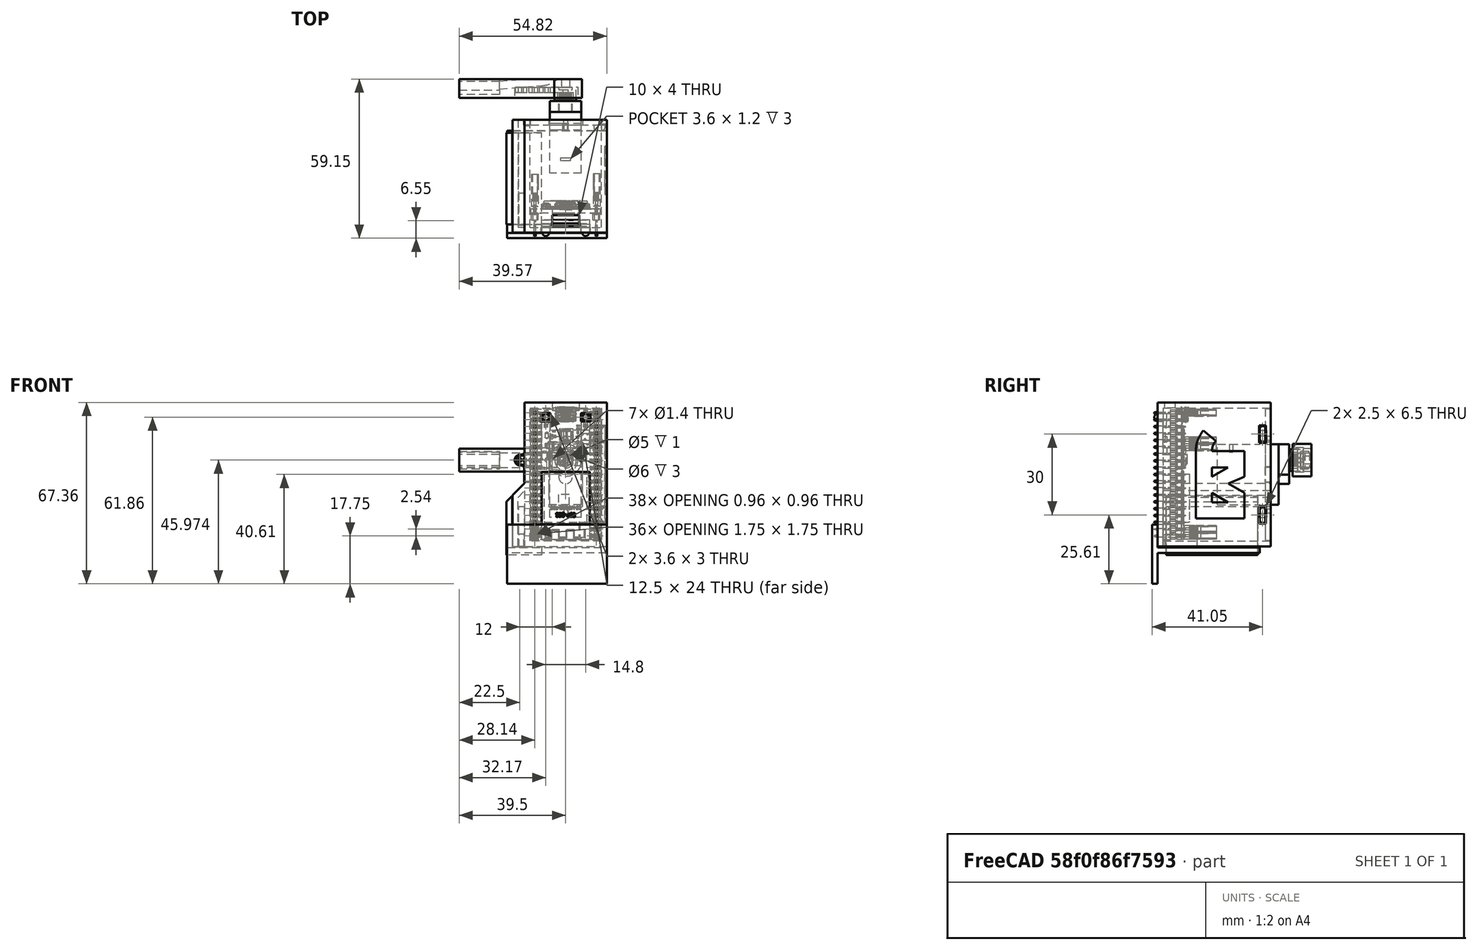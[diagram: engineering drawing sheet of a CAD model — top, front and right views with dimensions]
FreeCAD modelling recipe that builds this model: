
FCSTD DOCUMENT  (FreeCAD 0.18.4R)
Label: catdrainer_freecad
License: CreativeCommons Attribution-ShareAlike
LicenseURL: http://creativecommons.org/licenses/by-sa/4.0/
objects: Part::Feature×72, Sketcher::SketchObject×27, PartDesign::Pad×16, PartDesign::Pocket×11, PartDesign::Body×7, App::Part×2, Part::MultiFuse×2, PartDesign::AdditiveSphere×2, PartDesign::Fillet×1, Part::FeaturePython×1, Mesh::Feature×1, PartDesign::SubtractivePipe×1
note: 170 computed .brp shape members not serialized (recipe doc carries the construction recipe); baked Part::Feature solids carry a one-line shape summary decoded from their .brp

FEATURE [Part::Feature] Shape
  Placement = pos=(0.05,-0.05,0.75) rot=(0,0,1;0rad)
  shape: bbox 11.8 x 32.4 x 29.9 mm, 77 faces (baked)
FEATURE [Part::Feature] Part__Feature  label="ESP32S HW-573 PCB"
  shape: bbox 25.91 x 1.64 x 48.51 mm, 2018 faces (baked)
FEATURE [Part::Feature] Part__Feature001  label="ESP-WROOM-32"
  Placement = pos=(3e-15,1.565,-11.507) rot=(0,0.707107,0.707107;3.14159rad)
  shape: bbox 18.07 x 3.035 x 25.54 mm, 933 faces (baked)
FEATURE [Part::Feature] Part__Feature002  label="Male Header 19P 100 Pitch"
  Placement = pos=(11.43,-0.5,-0.005) rot=(0.57735,-0.57735,0.57735;2.0944rad)
  shape: bbox 2.54 x 11.54 x 47.96 mm, 648 faces (baked)
FEATURE [Part::Feature] Part__Feature003  label="Male Header 19P 100 Pitch001"
  Placement = pos=(-11.43,-0.5,-0.005) rot=(0.57735,-0.57735,0.57735;2.0944rad)
  shape: bbox 2.54 x 11.54 x 47.96 mm, 648 faces (baked)
FEATURE [Part::Feature] Part__Feature004  label="micro_usb_47346-0001"
  Placement = pos=(-1e-15,2.825,22.277) rot=(0,0,1;0rad)
  shape: bbox 7.98 x 2.94 x 5.43 mm, 394 faces (baked)
FEATURE [Part::Feature] Part__Feature005  label="CircuitWorks-SOT-223"
  Placement = pos=(4.374,2.38,6.453) rot=(0,1,0;1.5708rad)
  shape: bbox 6.96 x 1.68 x 6.5 mm, 86 faces (baked)
FEATURE [Part::Feature] Part__Feature006  label="Pol Cap SMD 3528 H2mm"
  Placement = pos=(-1.53686,1.6,5.5499) rot=(0,1,0;3.14159rad)
  shape: bbox 3.073 x 2.134 x 3.734 mm, 42 faces (baked)
FEATURE [Part::Feature] Part__Feature007  label="0805 SMD Capacitor"
  Placement = pos=(-6.069,1.6,6.903) rot=(0,-1,0;1.5708rad)
  shape: bbox 1.25 x 0.782 x 2 mm, 90 faces (baked)
FEATURE [Part::Feature] Part__Feature008  label="0603 SMD Resistor"
  Placement = pos=(-4.444,1.6,6.383) rot=(0,-1,0;1.5708rad)
  shape: bbox 0.8 x 0.302 x 1.6 mm, 90 faces (baked)
FEATURE [Part::Feature] Part__Feature009  label="SOT-23"
  Placement = pos=(7.19337,2.15,12.053) rot=(0,0,1;0rad)
  shape: bbox 3 x 1.1 x 2.5 mm, 49 faces (baked)
FEATURE [Part::Feature] Part__Feature010  label="QFN28_5X5"
  Placement = pos=(0.202,1.6,14.385) rot=(-0.57735,-0.57735,-0.57735;2.0944rad)
  shape: bbox 5.008 x 0.9445 x 5.008 mm, 254 faces, 31 solids (baked)
FEATURE [Part::Feature] Part__Feature011  label="SOT-024"
  Placement = pos=(7.19337,2.15,15.8743) rot=(0,0,1;0rad)
  shape: bbox 3 x 1.1 x 2.5 mm, 49 faces (baked)
FEATURE [Part::Feature] Part__Feature012  label="Tact Switch SMD Tab 4mmx3mm"
  Placement = pos=(-7.25,1.65,21.257) rot=(0,-1,0;1.5708rad)
  shape: bbox 3.001 x 2.301 x 5.001 mm, 101 faces, 3 solids (baked)
FEATURE [Part::Feature] Part__Feature013  label="Tact Switch SMD Tab 4mmx3mm001"
  Placement = pos=(7.35,1.65,21.257) rot=(0,-1,0;1.5708rad)
  shape: bbox 3.001 x 2.301 x 5.001 mm, 101 faces, 3 solids (baked)
FEATURE [Part::Feature] Part__Feature014  label="0402 SMD Resistor___ _________"
  Placement = pos=(4.684,1.58,10.4458) rot=(0,0,1;0rad)
  shape: bbox 1.042 x 0.3419 x 0.6019 mm, 289 faces, 3 solids (baked)
FEATURE [Part::Feature] Part__Feature015  label="0402 SMD Resistor___ _________001"
  Placement = pos=(4.684,1.58,18.0958) rot=(0,0,1;0rad)
  shape: bbox 1.042 x 0.3419 x 0.6019 mm, 289 faces, 3 solids (baked)
FEATURE [Part::Feature] Part__Feature016  label="0402 SMD Resistor___ _________002"
  Placement = pos=(4.684,1.58,16.9958) rot=(0,0,1;0rad)
  shape: bbox 1.042 x 0.3419 x 0.6019 mm, 289 faces, 3 solids (baked)
FEATURE [Part::Feature] Part__Feature017  label="0402 SMD Resistor___ _________003"
  Placement = pos=(4.514,1.58,15.5758) rot=(0,-1,0;1.5708rad)
  shape: bbox 0.6019 x 0.3419 x 1.042 mm, 289 faces, 3 solids (baked)
FEATURE [Part::Feature] Part__Feature018  label="0402 SMD Resistor___ _________004"
  Placement = pos=(4.514,1.58,12.0958) rot=(0,-1,0;1.5708rad)
  shape: bbox 0.6019 x 0.3419 x 1.042 mm, 289 faces, 3 solids (baked)
FEATURE [Part::Feature] Part__Feature019  label="0402 SMD Resistor___ _________005"
  Placement = pos=(4.514,1.58,13.8358) rot=(0,-1,0;1.5708rad)
  shape: bbox 0.6019 x 0.3419 x 1.042 mm, 289 faces, 3 solids (baked)
FEATURE [Part::Feature] Part__Feature020  label="LED SMD0603"
  Placement = pos=(-4.68116,1.59523,10.2006) rot=(-1,0,0;1.5708rad)
  shape: bbox 0.725 x 0.675 x 1.65 mm, 50 faces, 5 solids (baked)
FEATURE [Part::Feature] Part__Feature021  label="LED SMD0604"
  Placement = pos=(-7.23616,1.59523,10.2006) rot=(-1,0,0;1.5708rad)
  shape: bbox 0.725 x 0.675 x 1.65 mm, 50 faces, 5 solids (baked)
FEATURE [Part::Feature] Part__Feature022  label="0402 SMD Resistor___ _________006"
  Placement = pos=(-6.279,1.58,11.573) rot=(0,-1,0;1.5708rad)
  shape: bbox 0.6019 x 0.3419 x 1.042 mm, 289 faces, 3 solids (baked)
FEATURE [Part::Feature] Part__Feature023  label="0402 SMD Capacitor"
  Placement = pos=(-2.454,1.6,10.4668) rot=(0,0,1;0rad)
  shape: bbox 1 x 0.202 x 0.6 mm, 84 faces (baked)
FEATURE [Part::Feature] Part__Feature024  label="0402 SMD Resistor___ _________007"
  Placement = pos=(-2.434,1.6,9.3668) rot=(0,0,1;0rad)
  shape: bbox 1.042 x 0.3419 x 0.6019 mm, 289 faces, 3 solids (baked)
FEATURE [Part::Feature] Part__Feature025  label="0603 SMD Capacitor"
  Placement = pos=(-5.12,1.6,14.117) rot=(0,-1,0;1.5708rad)
  shape: bbox 0.8 x 0.302 x 1.6 mm, 90 faces (baked)
FEATURE [Part::Feature] Part__Feature026  label="0402 SMD Resistor___ _________008"
  Placement = pos=(-4.37,1.58,16.077) rot=(0,0,1;0rad)
  shape: bbox 1.042 x 0.3419 x 0.6019 mm, 289 faces, 3 solids (baked)
FEATURE [Part::Feature] Part__Feature027  label="0402 SMD Capacitor001"
  Placement = pos=(-3.9,1.6,14.097) rot=(0,1,0;1.5708rad)
  shape: bbox 0.6 x 0.202 x 1 mm, 84 faces (baked)
FEATURE [Part::Feature] Part__Feature028  label="SOD323F-1"
  Placement = pos=(-7.029,1.6,14.543) rot=(0.57735,-0.57735,-0.57735;4.18879rad)
  shape: bbox 1.35 x 1 x 2.5 mm, 29 faces (baked)
FEATURE [Part::Feature] Part__Feature029  label="Pin Solder Joint"
  Placement = pos=(11.43,1.62,22.86) rot=(0,0,1;0rad)
  shape: bbox 1.5 x 1.1 x 3 mm, 4 faces (baked)
FEATURE [Part::Feature] Part__Feature030  label="Pin Solder Joint001"
  Placement = pos=(-11.43,1.62,22.86) rot=(0,0,1;0rad)
  shape: bbox 1.5 x 1.1 x 3 mm, 4 faces (baked)
FEATURE [Part::Feature] Part__Feature031  label="Pin Solder Joint002"
  Placement = pos=(11.43,1.62,20.32) rot=(0,0,1;0rad)
  shape: bbox 1.5 x 1.1 x 3 mm, 4 faces (baked)
FEATURE [Part::Feature] Part__Feature032  label="Pin Solder Joint003"
  Placement = pos=(-11.43,1.62,20.32) rot=(0,0,1;0rad)
  shape: bbox 1.5 x 1.1 x 3 mm, 4 faces (baked)
FEATURE [Part::Feature] Part__Feature033  label="Pin Solder Joint004"
  Placement = pos=(11.43,1.62,17.78) rot=(0,0,1;0rad)
  shape: bbox 1.5 x 1.1 x 3 mm, 4 faces (baked)
FEATURE [Part::Feature] Part__Feature034  label="Pin Solder Joint005"
  Placement = pos=(-11.43,1.62,17.78) rot=(0,0,1;0rad)
  shape: bbox 1.5 x 1.1 x 3 mm, 4 faces (baked)
FEATURE [Part::Feature] Part__Feature035  label="Pin Solder Joint006"
  Placement = pos=(11.43,1.62,15.24) rot=(0,0,1;0rad)
  shape: bbox 1.5 x 1.1 x 3 mm, 4 faces (baked)
FEATURE [Part::Feature] Part__Feature036  label="Pin Solder Joint007"
  Placement = pos=(-11.43,1.62,15.24) rot=(0,0,1;0rad)
  shape: bbox 1.5 x 1.1 x 3 mm, 4 faces (baked)
FEATURE [Part::Feature] Part__Feature037  label="Pin Solder Joint008"
  Placement = pos=(11.43,1.62,12.7) rot=(0,0,1;0rad)
  shape: bbox 1.5 x 1.1 x 3 mm, 4 faces (baked)
FEATURE [Part::Feature] Part__Feature038  label="Pin Solder Joint009"
  Placement = pos=(-11.43,1.62,12.7) rot=(0,0,1;0rad)
  shape: bbox 1.5 x 1.1 x 3 mm, 4 faces (baked)
FEATURE [Part::Feature] Part__Feature039  label="Pin Solder Joint010"
  Placement = pos=(11.43,1.62,10.16) rot=(0,0,1;0rad)
  shape: bbox 1.5 x 1.1 x 3 mm, 4 faces (baked)
FEATURE [Part::Feature] Part__Feature040  label="Pin Solder Joint011"
  Placement = pos=(-11.43,1.62,10.16) rot=(0,0,1;0rad)
  shape: bbox 1.5 x 1.1 x 3 mm, 4 faces (baked)
FEATURE [Part::Feature] Part__Feature041  label="Pin Solder Joint012"
  Placement = pos=(11.43,1.62,7.62) rot=(0,0,1;0rad)
  shape: bbox 1.5 x 1.1 x 3 mm, 4 faces (baked)
FEATURE [Part::Feature] Part__Feature042  label="Pin Solder Joint013"
  Placement = pos=(-11.43,1.62,7.62) rot=(0,0,1;0rad)
  shape: bbox 1.5 x 1.1 x 3 mm, 4 faces (baked)
FEATURE [Part::Feature] Part__Feature043  label="Pin Solder Joint014"
  Placement = pos=(11.43,1.62,5.08) rot=(0,0,1;0rad)
  shape: bbox 1.5 x 1.1 x 3 mm, 4 faces (baked)
FEATURE [Part::Feature] Part__Feature044  label="Pin Solder Joint015"
  Placement = pos=(-11.43,1.62,5.08) rot=(0,0,1;0rad)
  shape: bbox 1.5 x 1.1 x 3 mm, 4 faces (baked)
FEATURE [Part::Feature] Part__Feature045  label="Pin Solder Joint016"
  Placement = pos=(11.43,1.62,2.54) rot=(0,0,1;0rad)
  shape: bbox 1.5 x 1.1 x 3 mm, 4 faces (baked)
FEATURE [Part::Feature] Part__Feature046  label="Pin Solder Joint017"
  Placement = pos=(-11.43,1.62,2.54) rot=(0,0,1;0rad)
  shape: bbox 1.5 x 1.1 x 3 mm, 4 faces (baked)
FEATURE [Part::Feature] Part__Feature047  label="Pin Solder Joint018"
  Placement = pos=(11.43,1.62,-3e-15) rot=(0,0,1;0rad)
  shape: bbox 1.5 x 1.1 x 3 mm, 4 faces (baked)
FEATURE [Part::Feature] Part__Feature048  label="Pin Solder Joint019"
  Placement = pos=(-11.43,1.62,-3e-15) rot=(0,0,1;0rad)
  shape: bbox 1.5 x 1.1 x 3 mm, 4 faces (baked)
FEATURE [Part::Feature] Part__Feature049  label="Pin Solder Joint020"
  Placement = pos=(11.43,1.62,-2.54) rot=(0,0,1;0rad)
  shape: bbox 1.5 x 1.1 x 3 mm, 4 faces (baked)
FEATURE [Part::Feature] Part__Feature050  label="Pin Solder Joint021"
  Placement = pos=(-11.43,1.62,-2.54) rot=(0,0,1;0rad)
  shape: bbox 1.5 x 1.1 x 3 mm, 4 faces (baked)
FEATURE [Part::Feature] Part__Feature051  label="Pin Solder Joint022"
  Placement = pos=(11.43,1.62,-5.08) rot=(0,0,1;0rad)
  shape: bbox 1.5 x 1.1 x 3 mm, 4 faces (baked)
FEATURE [Part::Feature] Part__Feature052  label="Pin Solder Joint023"
  Placement = pos=(-11.43,1.62,-5.08) rot=(0,0,1;0rad)
  shape: bbox 1.5 x 1.1 x 3 mm, 4 faces (baked)
FEATURE [Part::Feature] Part__Feature053  label="Pin Solder Joint024"
  Placement = pos=(11.43,1.62,-7.62) rot=(0,0,1;0rad)
  shape: bbox 1.5 x 1.1 x 3 mm, 4 faces (baked)
FEATURE [Part::Feature] Part__Feature054  label="Pin Solder Joint025"
  Placement = pos=(-11.43,1.62,-7.62) rot=(0,0,1;0rad)
  shape: bbox 1.5 x 1.1 x 3 mm, 4 faces (baked)
FEATURE [Part::Feature] Part__Feature055  label="Pin Solder Joint026"
  Placement = pos=(11.43,1.62,-10.16) rot=(0,0,1;0rad)
  shape: bbox 1.5 x 1.1 x 3 mm, 4 faces (baked)
FEATURE [Part::Feature] Part__Feature056  label="Pin Solder Joint027"
  Placement = pos=(-11.43,1.62,-10.16) rot=(0,0,1;0rad)
  shape: bbox 1.5 x 1.1 x 3 mm, 4 faces (baked)
FEATURE [Part::Feature] Part__Feature057  label="Pin Solder Joint028"
  Placement = pos=(11.43,1.62,-12.7) rot=(0,0,1;0rad)
  shape: bbox 1.5 x 1.1 x 3 mm, 4 faces (baked)
FEATURE [Part::Feature] Part__Feature058  label="Pin Solder Joint029"
  Placement = pos=(-11.43,1.62,-12.7) rot=(0,0,1;0rad)
  shape: bbox 1.5 x 1.1 x 3 mm, 4 faces (baked)
FEATURE [Part::Feature] Part__Feature059  label="Pin Solder Joint030"
  Placement = pos=(11.43,1.62,-15.24) rot=(0,0,1;0rad)
  shape: bbox 1.5 x 1.1 x 3 mm, 4 faces (baked)
FEATURE [Part::Feature] Part__Feature060  label="Pin Solder Joint031"
  Placement = pos=(-11.43,1.62,-15.24) rot=(0,0,1;0rad)
  shape: bbox 1.5 x 1.1 x 3 mm, 4 faces (baked)
FEATURE [Part::Feature] Part__Feature061  label="Pin Solder Joint032"
  Placement = pos=(11.43,1.62,-17.78) rot=(0,0,1;0rad)
  shape: bbox 1.5 x 1.1 x 3 mm, 4 faces (baked)
FEATURE [Part::Feature] Part__Feature062  label="Pin Solder Joint033"
  Placement = pos=(-11.43,1.62,-17.78) rot=(0,0,1;0rad)
  shape: bbox 1.5 x 1.1 x 3 mm, 4 faces (baked)
FEATURE [Part::Feature] Part__Feature063  label="Pin Solder Joint034"
  Placement = pos=(11.43,1.62,-20.32) rot=(0,0,1;0rad)
  shape: bbox 1.5 x 1.1 x 3 mm, 4 faces (baked)
FEATURE [Part::Feature] Part__Feature064  label="Pin Solder Joint035"
  Placement = pos=(-11.43,1.62,-20.32) rot=(0,0,1;0rad)
  shape: bbox 1.5 x 1.1 x 3 mm, 4 faces (baked)
FEATURE [Part::Feature] Part__Feature065  label="Pin Solder Joint036"
  Placement = pos=(11.43,1.62,-22.86) rot=(0,0,1;0rad)
  shape: bbox 1.5 x 1.1 x 3 mm, 4 faces (baked)
FEATURE [Part::Feature] Part__Feature066  label="Pin Solder Joint037"
  Placement = pos=(-11.43,1.62,-22.86) rot=(0,0,1;0rad)
  shape: bbox 1.5 x 1.1 x 3 mm, 4 faces (baked)
FEATURE [App::Part] ESP32S_Dev_Board_0_9inch_width_ASSY  label="ESP32S Dev Board 0.9inch width ASSY"
  Group = -> [Part__Feature,Part__Feature001,Part__Feature002,Part__Feature003,Part__Feature004,Part__Feature005,Part__Feature006,Part__Feature007,Part__Feature008,Part__Feature009,Part__Feature010,Part__Feature011,Part__Feature012,Part__Feature013,Part__Feature014,Part__Feature015,Part__Feature016,Part__Feature017,Part__Feature018,Part__Feature019,Part__Feature020,Part__Feature021,Part__Feature022,+44 more]
  Origin = -> Origin
  Placement = pos=(0,0,0) rot=(0,0,1;3.14159rad)
FEATURE [Part::Feature] Shape003  label="5v"
  Placement = pos=(-11.45,-14.6,22.9) rot=(0.57735,0.57735,0.57735;4.18879rad)
  shape: bbox 2.54 x 12 x 2.54 mm, 49 faces, 2 solids (baked)
FEATURE [Part::Feature] Shape006  label="laserplug"
  Placement = pos=(11.45,-14.55,-20.3) rot=(0.57735,-0.57735,-0.57735;4.18879rad)
  shape: bbox 2.54 x 12 x 5.08 mm, 98 faces, 4 solids (baked)
FEATURE [Part::Feature] Shape005  label="Servoplug"
  Placement = pos=(-11.45,-14.6,10.15) rot=(0.57735,0.57735,0.57735;4.18879rad)
  shape: bbox 2.54 x 12 x 5.08 mm, 98 faces, 4 solids (baked)
FEATURE [Part::MultiFuse] Fusion  label="pins"
  Placement = pos=(0,0,0) rot=(0,0,1;3.14159rad)
  Refine = true
  Shapes = -> [Shape006,Shape003,Shape005]
FEATURE [Sketcher::SketchObject] Sketch
  MapMode = 5
  Placement = pos=(0,0,0) rot=(0.57735,0.57735,0.57735;2.0944rad)
  Support = -> [YZ_Plane002]
  sketch-geometry (7):
    g0: LineSegment StartX=-4 StartY=22.5 StartZ=0 EndX=-4 EndY=20 EndZ=0
    g1: LineSegment StartX=-4 StartY=20 StartZ=0 EndX=-4.75 EndY=10 EndZ=0
    g2: LineSegment StartX=-4.75 StartY=10 StartZ=0 EndX=-5.25 EndY=10 EndZ=0
    g3: LineSegment StartX=-4 StartY=22.5 StartZ=0 EndX=-7.25 EndY=22.5 EndZ=0
    g4: LineSegment StartX=-5.25 StartY=10 StartZ=0 EndX=-5.25 EndY=20 EndZ=0
    g5: LineSegment StartX=-5.25 StartY=20 StartZ=0 EndX=-7.25 EndY=20 EndZ=0
    g6: LineSegment StartX=-7.25 StartY=20 StartZ=0 EndX=-7.25 EndY=22.5 EndZ=0
  constraints (21):
    c: Vertical(g0)
    c: Coincident(g0,g1)
    c: Coincident(g1,g2)
    c: Horizontal(g2)
    c: Coincident(g3,g0)
    c: Horizontal(g3)
    c: DistanceY(g0,g0) = 2.5
    c: DistanceX(g2,g2) = 0.5
    c: DistanceX(g3,g3) = 3.25
    c: DistanceX(g1) = -4.75
    c: DistanceY(g1) = 10
    c: Coincident(g2,g4)
    c: Vertical(g4)
    c: Coincident(g4,g5)
    c: Horizontal(g5)
    c: Coincident(g5,g6)
    c: Vertical(g6)
    c: DistanceX(g5,g5) = 2
    c: Coincident(g3,g6)
    c: DistanceY(g6,g6) = 2.5
    c: DistanceY(g4,g4) = 10
FEATURE [PartDesign::Pad] Pad
  Length = 18
  Length2 = 100
  Midplane = true
  Placement = pos=(0,0,0) rot=(0.57735,0.57735,0.57735;2.0944rad)
  Profile = -> Sketch
  Refine = true
  Type = 0
FEATURE [Sketcher::SketchObject] Sketch001
  ExternalGeometry = -> [Pad]
  MapMode = 5
  Placement = pos=(-3.2e-15,-7.25,1.6e-15) rot=(-0.57735,-0.57735,0.57735;4.18879rad)
  Support = -> [Pad]
  sketch-geometry (4):
    g0: LineSegment StartX=-22.5 StartY=5.8 StartZ=0 EndX=-12 EndY=5.8 EndZ=0
    g1: LineSegment StartX=-12 StartY=5.8 StartZ=0 EndX=-12 EndY=-5.8 EndZ=0
    g2: LineSegment StartX=-12 StartY=-5.8 StartZ=0 EndX=-22.5 EndY=-5.8 EndZ=0
    g3: LineSegment StartX=-22.5 StartY=-5.8 StartZ=0 EndX=-22.5 EndY=5.8 EndZ=0
  constraints (11):
    c: Coincident(g0,g1)
    c: Coincident(g1,g2)
    c: Coincident(g2,g3)
    c: Coincident(g3,g0)
    c: Horizontal(g0)
    c: Horizontal(g2)
    c: Vertical(g1)
    c: Distance(g1,g-3) = 2
    c: Symmetric(g0,g2,g-1)
    c: DistanceY(g-4,g2) = 3.2
    c: PointOnObject(g2,g-5)
FEATURE [PartDesign::Pocket] Pocket
  BaseFeature = -> Pad
  Length = 5
  Length2 = 100
  Placement = pos=(0,0,0) rot=(0.57735,0.57735,0.57735;2.0944rad)
  Profile = -> Sketch001
  Refine = true
  Type = 0
FEATURE [Sketcher::SketchObject] Sketch002
  MapMode = 5
  Placement = pos=(-3e-15,-7.25,5e-15) rot=(0.57735,0.57735,-0.57735;2.0944rad)
  sketch-geometry (16):
    g0: LineSegment StartX=-26.75 StartY=15.25 StartZ=0 EndX=-26.75 EndY=-15.25 EndZ=0
    g1: LineSegment StartX=-26.75 StartY=-15.25 StartZ=0 EndX=26.75 EndY=-15.25 EndZ=0
    g2: LineSegment StartX=26.75 StartY=-15.25 StartZ=0 EndX=26.75 EndY=15.25 EndZ=0
    g3: LineSegment StartX=26.75 StartY=15.25 StartZ=0 EndX=-26.75 EndY=15.25 EndZ=0
    g4: LineSegment StartX=-1 StartY=9 StartZ=0 EndX=18.5 EndY=9 EndZ=0
    g5: LineSegment StartX=18.5 StartY=9 StartZ=0 EndX=18.5 EndY=-9 EndZ=0
    g6: LineSegment StartX=18.5 StartY=-9 StartZ=0 EndX=-1 EndY=-9 EndZ=0
    g7: LineSegment StartX=-1 StartY=-9 StartZ=0 EndX=-1 EndY=9 EndZ=0
    g8: LineSegment StartX=-22.75 StartY=9.2 StartZ=0 EndX=-19.75 EndY=9.2 EndZ=0
    g9: LineSegment StartX=-19.75 StartY=9.2 StartZ=0 EndX=-19.75 EndY=5.6 EndZ=0
    g10: LineSegment StartX=-19.75 StartY=5.6 StartZ=0 EndX=-22.75 EndY=5.6 EndZ=0
    g11: LineSegment StartX=-22.75 StartY=5.6 StartZ=0 EndX=-22.75 EndY=9.2 EndZ=0
    g12: LineSegment StartX=-22.75 StartY=-5.6 StartZ=0 EndX=-19.75 EndY=-5.6 EndZ=0
    g13: LineSegment StartX=-19.75 StartY=-5.6 StartZ=0 EndX=-19.75 EndY=-9.2 EndZ=0
    g14: LineSegment StartX=-19.75 StartY=-9.2 StartZ=0 EndX=-22.75 EndY=-9.2 EndZ=0
    g15: LineSegment StartX=-22.75 StartY=-9.2 StartZ=0 EndX=-22.75 EndY=-5.6 EndZ=0
  constraints (44):
    c: Coincident(g0,g1)
    c: Horizontal(g1)
    c: Coincident(g1,g2)
    c: Vertical(g2)
    c: Coincident(g2,g3)
    c: Coincident(g0,g3)
    c: Symmetric(g0,g0,g-1)
    c: DistanceY(g0,g0) = 30.5
    c: DistanceX(g3,g3) = 53.5
    c: Coincident(g5,g6)
    c: Coincident(g6,g7)
    c: Coincident(g7,g4)
    c: Horizontal(g4)
    c: Horizontal(g6)
    c: Vertical(g7)
    c: Symmetric(g4,g5,g-1)
    c: DistanceY(g4) = 9
    c: Coincident(g4,g5)
    c: DistanceX(g6,g6) = 19.5
    c: Coincident(g8,g9)
    c: Coincident(g9,g10)
    c: Coincident(g10,g11)
    c: Coincident(g11,g8)
    c: Horizontal(g8)
    c: Horizontal(g10)
    c: Vertical(g9)
    c: Vertical(g11)
    c: Coincident(g12,g13)
    c: Coincident(g13,g14)
    c: Coincident(g14,g15)
    c: Coincident(g15,g12)
    c: Horizontal(g12)
    c: Horizontal(g14)
    c: Vertical(g13)
    c: Vertical(g15)
    c: Symmetric(g9,g12,g-1)
    c: DistanceY(g13,g13) = 3.6
    c: DistanceY(g12) = -5.6
    c: DistanceX(g12,g12) = 3
    c: Equal(g15,g11)
    c: Equal(g12,g8)
    c: Symmetric(g2,g0,g-2)
    c: DistanceX(g12,g-1) = 19.75
    c: DistanceX(g6,g-1) = 1
FEATURE [PartDesign::Pad] Pad001  label="Base"
  Length = 2
  Length2 = 100
  Placement = pos=(-3e-15,-7.25,5e-15) rot=(0.57735,0.57735,-0.57735;2.0944rad)
  Profile = -> Sketch002
  Refine = true
  Reversed = true
  Type = 0
FEATURE [Sketcher::SketchObject] Sketch003
  ExternalGeometry = -> [Pad001]
  MapMode = 5
  Placement = pos=(1.4e-15,-5.25,4.3e-15) rot=(-0.57735,0.57735,0.57735;2.0944rad)
  Support = -> [Pad001]
  sketch-geometry (9):
    g0: LineSegment StartX=-14.15 StartY=-5.625 StartZ=0 EndX=-12.15 EndY=-5.625 EndZ=0
    g1: LineSegment StartX=-12.15 StartY=-5.625 StartZ=0 EndX=-12.15 EndY=5.625 EndZ=0
    g2: LineSegment StartX=-12.15 StartY=5.625 StartZ=0 EndX=-14.15 EndY=5.625 EndZ=0
    g3: LineSegment StartX=-14.15 StartY=5.625 StartZ=0 EndX=-14.15 EndY=-5.625 EndZ=0
    g4: LineSegment StartX=-9.9 StartY=-9 StartZ=0 EndX=-7.9 EndY=-9 EndZ=0
    g5: LineSegment StartX=-7.9 StartY=-9 StartZ=0 EndX=-7.9 EndY=9 EndZ=0
    g6: LineSegment StartX=-7.9 StartY=9 StartZ=0 EndX=-9.9 EndY=9 EndZ=0
    g7: LineSegment StartX=-9.9 StartY=9 StartZ=0 EndX=-9.9 EndY=-9 EndZ=0
    g8: LineSegment [constr] StartX=-12.15 StartY=5.625 StartZ=0 EndX=-9.9 EndY=5.625 EndZ=0
  constraints (25):
    c: Coincident(g0,g1)
    c: Coincident(g1,g2)
    c: Coincident(g2,g3)
    c: Coincident(g3,g0)
    c: Horizontal(g0)
    c: Horizontal(g2)
    c: Vertical(g3)
    c: Coincident(g4,g5)
    c: Coincident(g5,g6)
    c: Coincident(g6,g7)
    c: Coincident(g7,g4)
    c: Horizontal(g4)
    c: Horizontal(g6)
    c: Vertical(g7)
    c: Equal(g6,g2)
    c: DistanceX(g6,g6) = 2
    c: DistanceX(g5,g-3) = 6.9
    c: PointOnObject(g8,g7)
    c: Horizontal(g8)
    c: Symmetric(g4,g5,g-1)
    c: DistanceY(g5,g5) = 18
    c: Symmetric(g1,g0,g-1)
    c: DistanceY(g1,g1) = 11.25
    c: DistanceX(g8,g8) = 2.25
    c: Coincident(g8,g1)
FEATURE [PartDesign::Pad] Pad002  label="buton_tabs"
  BaseFeature = -> Pad001
  Length = 1.5
  Length2 = 100
  Placement = pos=(-3e-15,-7.25,5e-15) rot=(0.57735,0.57735,-0.57735;2.0944rad)
  Profile = -> Sketch003
  Refine = true
  Type = 0
FEATURE [Sketcher::SketchObject] Sketch004
  ExternalGeometry = -> [Pad002]
  MapMode = 5
  Placement = pos=(3.4e-15,-5.25,4.3e-15) rot=(-0.57735,0.57735,0.57735;2.0944rad)
  Support = -> [Pad002]
  sketch-geometry (5):
    g0: LineSegment StartX=18.5 StartY=9 StartZ=0 EndX=24.25 EndY=9 EndZ=0
    g1: LineSegment StartX=24.25 StartY=9 StartZ=0 EndX=24.25 EndY=-9 EndZ=0
    g2: LineSegment StartX=24.25 StartY=-9 StartZ=0 EndX=18.5 EndY=-9 EndZ=0
    g3: LineSegment StartX=18.5 StartY=-9 StartZ=0 EndX=18.5 EndY=9 EndZ=0
    g4: LineSegment [constr] StartX=24.25 StartY=9 StartZ=0 EndX=26.75 EndY=9 EndZ=0
  constraints (13):
    c: Coincident(g0,g1)
    c: Coincident(g1,g2)
    c: Coincident(g2,g3)
    c: Coincident(g3,g0)
    c: Horizontal(g0)
    c: Horizontal(g2)
    c: Vertical(g1)
    c: Coincident(g0,g-3)
    c: Coincident(g4,g0)
    c: PointOnObject(g4,g-4)
    c: Horizontal(g4)
    c: DistanceX(g4,g4) = 2.5
    c: Coincident(g2,g-3)
FEATURE [PartDesign::Pad] Pad003  label="antenna_bump"
  BaseFeature = -> Pad002
  Length = 2.75
  Length2 = 100
  Placement = pos=(-3e-15,-7.25,5e-15) rot=(0.57735,0.57735,-0.57735;2.0944rad)
  Profile = -> Sketch004
  Refine = true
  Type = 0
FEATURE [Sketcher::SketchObject] Sketch005
  ExternalGeometry = -> [Pad003]
  MapMode = 5
  Placement = pos=(5.4e-15,-5.25,4.3e-15) rot=(-0.57735,0.57735,0.57735;2.0944rad)
  Support = -> [Pad003]
  sketch-geometry (8):
    g0: LineSegment StartX=26.75 StartY=-15.25 StartZ=0 EndX=-26.75 EndY=-15.25 EndZ=0
    g1: LineSegment StartX=-26.75 StartY=-15.25 StartZ=0 EndX=-26.75 EndY=15.25 EndZ=0
    g2: LineSegment StartX=-26.75 StartY=15.25 StartZ=0 EndX=26.75 EndY=15.25 EndZ=0
    g3: LineSegment StartX=26.75 StartY=15.25 StartZ=0 EndX=26.75 EndY=-15.25 EndZ=0
    g4: LineSegment StartX=-24.75 StartY=-13.25 StartZ=0 EndX=24.75 EndY=-13.25 EndZ=0
    g5: LineSegment StartX=24.75 StartY=-13.25 StartZ=0 EndX=24.75 EndY=13.25 EndZ=0
    g6: LineSegment StartX=24.75 StartY=13.25 StartZ=0 EndX=-24.75 EndY=13.25 EndZ=0
    g7: LineSegment StartX=-24.75 StartY=13.25 StartZ=0 EndX=-24.75 EndY=-13.25 EndZ=0
  constraints (19):
    c: Coincident(g0,g1)
    c: Coincident(g1,g2)
    c: Coincident(g6,g7)
    c: Coincident(g5,g6)
    c: Coincident(g4,g5)
    c: Coincident(g4,g7)
    c: Coincident(g0,g3)
    c: Coincident(g2,g3)
    c: Coincident(g0,g-3)
    c: Coincident(g2,g-3)
    c: Coincident(g1,g-4)
    c: Coincident(g0,g-4)
    c: Vertical(g5)
    c: Horizontal(g6)
    c: Horizontal(g4)
    c: Vertical(g7)
    c: Symmetric(g6,g4,g-1)
    c: Distance(g5,g3) = 2
    c: DistanceY(g5,g2) = 2
FEATURE [PartDesign::Pad] Pad004  label="Walls"
  BaseFeature = -> Pad003
  Length = 40
  Length2 = 100
  Placement = pos=(-3e-15,-7.25,5e-15) rot=(0.57735,0.57735,-0.57735;2.0944rad)
  Profile = -> Sketch005
  Refine = true
  Type = 0
FEATURE [Sketcher::SketchObject] Sketch006
  MapMode = 5
  Placement = pos=(1.53493e-10,-7.25,26.75) rot=(0,0,1;3.14159rad)
  Support = -> [Pad004]
  sketch-geometry (4):
    g0: LineSegment StartX=-5 StartY=-2.5 StartZ=0 EndX=5 EndY=-2.5 EndZ=0
    g1: LineSegment StartX=5 StartY=-2.5 StartZ=0 EndX=5 EndY=-6.5 EndZ=0
    g2: LineSegment StartX=5 StartY=-6.5 StartZ=0 EndX=-5 EndY=-6.5 EndZ=0
    g3: LineSegment StartX=-5 StartY=-6.5 StartZ=0 EndX=-5 EndY=-2.5 EndZ=0
  constraints (11):
    c: Coincident(g0,g3)
    c: Coincident(g0,g1)
    c: Coincident(g1,g2)
    c: Coincident(g2,g3)
    c: DistanceY(g1,g1) = 4
    c: DistanceX(g2,g2) = 10
    c: Equal(g1,g3)
    c: Vertical(g1)
    c: Vertical(g3)
    c: Symmetric(g0,g0,g-2)
    c: DistanceY(g0,g-1) = 2.5
FEATURE [PartDesign::Pocket] Pocket001  label="USB Opening"
  BaseFeature = -> Pad004
  Length = 2
  Length2 = 100
  Placement = pos=(-3e-15,-7.25,5e-15) rot=(0.57735,0.57735,-0.57735;2.0944rad)
  Profile = -> Sketch006
  Refine = true
  Type = 0
FEATURE [Sketcher::SketchObject] Sketch008  label="two_lid_clips"
  ExternalGeometry = -> [Pocket001]
  MapMode = 5
  Placement = pos=(15.25,-7.25,-8.51e-12) rot=(0.707107,0,0.707107;3.14159rad)
  Support = -> [Pocket001]
  sketch-geometry (8):
    g0: LineSegment StartX=-18.25 StartY=-37.75 StartZ=0 EndX=-11.75 EndY=-37.75 EndZ=0
    g1: LineSegment StartX=-11.75 StartY=-37.75 StartZ=0 EndX=-11.75 EndY=-40.25 EndZ=0
    g2: LineSegment StartX=-11.75 StartY=-40.25 StartZ=0 EndX=-18.25 EndY=-40.25 EndZ=0
    g3: LineSegment StartX=-18.25 StartY=-40.25 StartZ=0 EndX=-18.25 EndY=-37.75 EndZ=0
    g4: LineSegment StartX=11.75 StartY=-37.75 StartZ=0 EndX=18.25 EndY=-37.75 EndZ=0
    g5: LineSegment StartX=18.25 StartY=-37.75 StartZ=0 EndX=18.25 EndY=-40.25 EndZ=0
    g6: LineSegment StartX=18.25 StartY=-40.25 StartZ=0 EndX=11.75 EndY=-40.25 EndZ=0
    g7: LineSegment StartX=11.75 StartY=-40.25 StartZ=0 EndX=11.75 EndY=-37.75 EndZ=0
  constraints (23):
    c: Coincident(g0,g1)
    c: Coincident(g1,g2)
    c: Coincident(g2,g3)
    c: Coincident(g3,g0)
    c: Horizontal(g0)
    c: Horizontal(g2)
    c: Vertical(g1)
    c: Vertical(g3)
    c: Coincident(g4,g5)
    c: Coincident(g5,g6)
    c: Coincident(g6,g7)
    c: Coincident(g7,g4)
    c: Horizontal(g4)
    c: Horizontal(g6)
    c: Vertical(g5)
    c: Vertical(g7)
    c: Equal(g4,g0)
    c: Equal(g7,g1)
    c: DistanceY(g5,g5) = 2.5
    c: DistanceX(g6,g6) = 6.5
    c: Symmetric(g6,g1,g-2)
    c: Distance(g5,g-3) = 1.75
    c: DistanceX(g1,g6) = 23.5
FEATURE [PartDesign::Pocket] Pocket002  label="lid_clip_opening"
  BaseFeature = -> Pocket001
  Length = 5
  Length2 = 100
  Placement = pos=(-3e-15,-7.25,5e-15) rot=(0.57735,0.57735,-0.57735;2.0944rad)
  Profile = -> Sketch008
  Refine = true
  Type = 0
FEATURE [Sketcher::SketchObject] Sketch009
  AttachmentOffset = pos=(0,0,32.75) rot=(0,0,1;0rad)
  MapMode = 5
  Placement = pos=(0,32.75,7.3e-15) rot=(0,0.707107,0.707107;3.14159rad)
  Support = -> [XZ_Plane004]
  sketch-geometry (9):
    g0: LineSegment StartX=13 StartY=24.5 StartZ=0 EndX=-13 EndY=24.5 EndZ=0
    g1: LineSegment StartX=-13 StartY=24.5 StartZ=0 EndX=-13 EndY=-24.5 EndZ=0
    g2: LineSegment StartX=-13 StartY=-24.5 StartZ=0 EndX=13 EndY=-24.5 EndZ=0
    g3: LineSegment StartX=13 StartY=24.5 StartZ=0 EndX=13 EndY=2.75 EndZ=0
    g4: LineSegment StartX=13 StartY=2.75 StartZ=0 EndX=15.4 EndY=2.75 EndZ=0
    g5: LineSegment StartX=15.4 StartY=2.75 StartZ=0 EndX=15.4 EndY=-2.75 EndZ=0
    g6: LineSegment StartX=15.4 StartY=-2.75 StartZ=0 EndX=13 EndY=-2.75 EndZ=0
    g7: LineSegment StartX=13 StartY=-2.75 StartZ=0 EndX=13 EndY=-24.5 EndZ=0
    g8: LineSegment [constr] StartX=13 StartY=2.75 StartZ=0 EndX=13 EndY=-2.75 EndZ=0
  constraints (24):
    c: Coincident(g0,g1)
    c: Coincident(g1,g2)
    c: Horizontal(g0)
    c: Horizontal(g2)
    c: Vertical(g1)
    c: Symmetric(g0,g2,g-1)
    c: DistanceX(g0,g0) = 26
    c: DistanceY(g1,g1) = 49
    c: Coincident(g0,g3)
    c: Vertical(g3)
    c: Coincident(g3,g4)
    c: Coincident(g4,g5)
    c: Coincident(g5,g6)
    c: Horizontal(g6)
    c: Coincident(g6,g7)
    c: Coincident(g7,g2)
    c: Vertical(g7)
    c: Horizontal(g4)
    c: DistanceY(g5,g5) = 5.5
    c: Symmetric(g4,g5,g-1)
    c: Coincident(g8,g3)
    c: Coincident(g8,g6)
    c: Vertical(g8)
    c: DistanceX(g4,g4) = 2.4
FEATURE [PartDesign::Pad] Pad005
  Length = 2
  Length2 = 100
  Placement = pos=(0,0,0) rot=(1,0,0;1.5708rad)
  Profile = -> Sketch009
  Refine = true
  Type = 0
FEATURE [Sketcher::SketchObject] Sketch010
  ExternalGeometry = -> [Pocket002]
  MapMode = 5
  Placement = pos=(-15.25,-7.25,7.599e-13) rot=(-0.707107,0,0.707107;3.14159rad)
  Support = -> [Pocket002]
  sketch-geometry (4):
    g0: LineSegment StartX=-2.875 StartY=-39.85 StartZ=0 EndX=2.875 EndY=-39.85 EndZ=0
    g1: LineSegment StartX=2.875 StartY=-39.85 StartZ=0 EndX=2.875 EndY=-42 EndZ=0
    g2: LineSegment StartX=2.875 StartY=-42 StartZ=0 EndX=-2.875 EndY=-42 EndZ=0
    g3: LineSegment StartX=-2.875 StartY=-42 StartZ=0 EndX=-2.875 EndY=-39.85 EndZ=0
  constraints (11):
    c: Coincident(g2,g3)
    c: Coincident(g1,g2)
    c: Coincident(g0,g3)
    c: Coincident(g0,g1)
    c: Symmetric(g0,g0,g-2)
    c: Vertical(g1)
    c: Vertical(g3)
    c: Horizontal(g2)
    c: DistanceX(g2,g2) = 5.75
    c: DistanceY(g1,g1) = 2.15
    c: PointOnObject(g1,g-3)
FEATURE [PartDesign::Pocket] Pocket003  label="Latch_tab_hole"
  BaseFeature = -> Pocket002
  Length = 5
  Length2 = 100
  Placement = pos=(-3e-15,-7.25,5e-15) rot=(0.57735,0.57735,-0.57735;2.0944rad)
  Profile = -> Sketch010
  Refine = true
  Type = 0
FEATURE [Sketcher::SketchObject] Sketch011
  ExternalGeometry = -> [Pad005]
  MapMode = 5
  Placement = pos=(0,32.75,-9.5e-15) rot=(1,0,0;1.5708rad)
  Support = -> [Pad005]
  sketch-geometry (8):
    g0: LineSegment StartX=10.5 StartY=18 StartZ=0 EndX=12.5 EndY=18 EndZ=0
    g1: LineSegment StartX=12.5 StartY=18 StartZ=0 EndX=12.5 EndY=12 EndZ=0
    g2: LineSegment StartX=12.5 StartY=12 StartZ=0 EndX=10.5 EndY=12 EndZ=0
    g3: LineSegment StartX=10.5 StartY=12 StartZ=0 EndX=10.5 EndY=18 EndZ=0
    g4: LineSegment StartX=10.5 StartY=-12 StartZ=0 EndX=12.5 EndY=-12 EndZ=0
    g5: LineSegment StartX=12.5 StartY=-12 StartZ=0 EndX=12.5 EndY=-18 EndZ=0
    g6: LineSegment StartX=12.5 StartY=-18 StartZ=0 EndX=10.5 EndY=-18 EndZ=0
    g7: LineSegment StartX=10.5 StartY=-18 StartZ=0 EndX=10.5 EndY=-12 EndZ=0
  constraints (23):
    c: Coincident(g0,g1)
    c: Coincident(g1,g2)
    c: Coincident(g2,g3)
    c: Coincident(g3,g0)
    c: Horizontal(g0)
    c: Horizontal(g2)
    c: Vertical(g1)
    c: Vertical(g3)
    c: Coincident(g4,g5)
    c: Coincident(g5,g6)
    c: Coincident(g6,g7)
    c: Coincident(g7,g4)
    c: Horizontal(g4)
    c: Horizontal(g6)
    c: Vertical(g5)
    c: Vertical(g7)
    c: Symmetric(g1,g4,g-1)
    c: DistanceY(g4,g1) = 24
    c: Equal(g1,g5)
    c: Equal(g0,g4)
    c: DistanceY(g1,g1) = 6
    c: DistanceX(g0,g0) = 2
    c: Distance(g0,g-3) = 0.5
FEATURE [PartDesign::Pad] Pad006
  BaseFeature = -> Pad005
  Length = 2
  Length2 = 100
  Placement = pos=(0,0,0) rot=(1,0,0;1.5708rad)
  Profile = -> Sketch011
  Refine = true
  Type = 0
FEATURE [PartDesign::Pad] Pad007
  BaseFeature = -> Pad006
  Length = 2
  Length2 = 100
  Placement = pos=(0,0,0) rot=(1,0,0;1.5708rad)
  Profile = -> Pad006 [Face12]
  Refine = true
  Type = 0
FEATURE [PartDesign::Pad] Pad008
  BaseFeature = -> Pad007
  Length = 2
  Length2 = 100
  Placement = pos=(0,0,0) rot=(1,0,0;1.5708rad)
  Profile = -> Pad007 [Face15]
  Refine = true
  Type = 0
FEATURE [PartDesign::Fillet] Fillet
  Base = -> Pad008 [Edge54,Edge51,Edge48,Edge43,Edge49,Edge45,Edge56,Edge55]
  BaseFeature = -> Pad008
  Placement = pos=(0,0,0) rot=(1,0,0;1.5708rad)
  Radius = 1
FEATURE [Sketcher::SketchObject] Sketch012
  MapMode = 5
  Placement = pos=(0,34.75,-1.01e-14) rot=(-1,0,0;1.5708rad)
  Support = -> [Fillet]
  sketch-geometry (6):
    g0: LineSegment StartX=-6.25 StartY=12 StartZ=0 EndX=6.25 EndY=12 EndZ=0
    g1: LineSegment StartX=6.25 StartY=12 StartZ=0 EndX=6.25 EndY=-12 EndZ=0
    g2: LineSegment StartX=6.25 StartY=-12 StartZ=0 EndX=-6.25 EndY=-12 EndZ=0
    g3: LineSegment StartX=-6.25 StartY=-12 StartZ=0 EndX=-6.25 EndY=12 EndZ=0
    g4: Circle CenterX=0 CenterY=13.5 CenterZ=0 NormalX=0 NormalY=0 NormalZ=1 AngleXU=0 Radius=0.75
    g5: Circle CenterX=0 CenterY=-13.5 CenterZ=0 NormalX=0 NormalY=0 NormalZ=1 AngleXU=0 Radius=0.75
  constraints (16):
    c: Coincident(g0,g1)
    c: Coincident(g1,g2)
    c: Coincident(g2,g3)
    c: Coincident(g3,g0)
    c: Horizontal(g0)
    c: Vertical(g1)
    c: Symmetric(g1,g2,g-2)
    c: Symmetric(g0,g2,g-1)
    c: DistanceY(g3,g3) = 24
    c: DistanceX(g0,g0) = 12.5
    c: PointOnObject(g4,g-2)
    c: Radius(g4) = 0.75
    c: DistanceY(g-1,g4) = 13.5
    c: PointOnObject(g5,g-2)
    c: Equal(g4,g5)
    c: DistanceY(g5,g-1) = 13.5
FEATURE [PartDesign::Pocket] Pocket004
  BaseFeature = -> Fillet
  Length = 5
  Length2 = 100
  Placement = pos=(0,0,0) rot=(1,0,0;1.5708rad)
  Profile = -> Sketch012
  Refine = true
  Type = 0
FEATURE [PartDesign::Body] Body002  label="Lid"
  Group = -> [Sketch009,Pad005,Sketch011,Pad006,Pad007,Pad008,Fillet,Sketch012,Pocket004]
  Origin = -> Origin004
  Tip = -> Pocket004
FEATURE [Sketcher::SketchObject] Sketch013  label="sigil"
  AttachmentOffset = pos=(-3,-17,0) rot=(0,0,1;3.14159rad)
  ExternalGeometry = -> [Pocket003]
  MapMode = 5
  Placement = pos=(15.25,9.75,-3) rot=(0,-1,0;4.71239rad)
  Support = -> [Pocket003]
  sketch-geometry (26):
    g0: LineSegment StartX=-11.6433 StartY=3.19253 StartZ=0 EndX=-11.6433 EndY=15.1925 EndZ=0
    g1: LineSegment StartX=-11.6433 StartY=15.1925 StartZ=0 EndX=-2.14327 EndY=15.1925 EndZ=0
    g2: LineSegment StartX=-2.14327 StartY=15.1925 StartZ=0 EndX=0.389061 EndY=9.21116 EndZ=0
    g3: LineSegment StartX=0.389061 StartY=9.21116 StartZ=0 EndX=3.85673 EndY=15.1925 EndZ=0
    g4: LineSegment StartX=3.85673 StartY=15.1925 StartZ=0 EndX=13.3567 EndY=15.1925 EndZ=0
    g5: LineSegment StartX=13.3567 StartY=15.1925 StartZ=0 EndX=13.3567 EndY=-2.80747 EndZ=0
    g6: LineSegment StartX=13.3567 StartY=-2.80747 StartZ=0 EndX=-11.6433 EndY=-2.80747 EndZ=0
    g7: ArcOfCircle CenterX=-11.6433 CenterY=9.19253 CenterZ=0 NormalX=0 NormalY=0 NormalZ=1 AngleXU=0 Radius=12 StartAngle=4.01426 EndAngle=4.71239
    g8: LineSegment StartX=-19.3567 StartY=-1.2501e-12 StartZ=0 EndX=-15.5 EndY=4.59627 EndZ=0
    g9: ArcOfCircle CenterX=-11.6433 CenterY=9.19253 CenterZ=0 NormalX=0 NormalY=0 NormalZ=1 AngleXU=0 Radius=6 StartAngle=4.01426 EndAngle=4.71239
    g10: LineSegment [constr] StartX=-11.6433 StartY=3.19253 StartZ=0 EndX=-11.6433 EndY=-2.80747 EndZ=0
    g11: LineSegment StartX=-5.64327 StartY=9.19253 StartZ=0 EndX=-5.64327 EndY=3.19253 EndZ=0
    g12: LineSegment StartX=-5.64327 StartY=3.19253 StartZ=0 EndX=-2.16481 EndY=3.19253 EndZ=0
    g13: LineSegment StartX=-2.16481 StartY=3.19253 StartZ=0 EndX=-5.64327 EndY=9.19253 EndZ=0
    g14: LineSegment StartX=7.31366 StartY=9.19253 StartZ=0 EndX=7.31366 EndY=3.19253 EndZ=0
    g15: LineSegment StartX=7.31366 StartY=3.19253 StartZ=0 EndX=3.83519 EndY=3.19253 EndZ=0
    g16: LineSegment StartX=3.83519 StartY=3.19253 StartZ=0 EndX=7.31366 EndY=9.19253 EndZ=0
    g17: LineSegment [constr] StartX=-5.64327 StartY=3.19253 StartZ=0 EndX=-11.6433 EndY=3.19253 EndZ=0
    g18: LineSegment [constr] StartX=-2.16481 StartY=3.19253 StartZ=0 EndX=3.83519 EndY=3.19253 EndZ=0
    g19: LineSegment [constr] StartX=7.31366 StartY=3.19253 StartZ=0 EndX=13.3137 EndY=3.19253 EndZ=0
    g20: LineSegment [constr] StartX=-5.64327 StartY=9.19253 StartZ=0 EndX=-5.64327 EndY=15.1925 EndZ=0
    g21: LineSegment [constr] StartX=7.31366 StartY=9.19253 StartZ=0 EndX=7.31366 EndY=15.1925 EndZ=0
    g22: LineSegment [constr] StartX=7.31366 StartY=9.19253 StartZ=0 EndX=2.12289 EndY=12.2018 EndZ=0
    g23: LineSegment [constr] StartX=3.85673 StartY=15.1925 StartZ=0 EndX=-2.14327 EndY=15.1925 EndZ=0
    g24: LineSegment [constr] StartX=-19.3567 StartY=-1.2501e-12 StartZ=0 EndX=13.3567 EndY=-1.2501e-12 EndZ=0
    g25: GeomPoint X=-3 Y=-7.8686e-12 Z=0
  constraints (70):
    c: Vertical(g0)
    c: Coincident(g0,g1)
    c: Horizontal(g1)
    c: Coincident(g1,g2)
    c: Coincident(g2,g3)
    c: Coincident(g3,g4)
    c: Coincident(g4,g5)
    c: Vertical(g5)
    c: Coincident(g5,g6)
    c: Horizontal(g6)
    c: Tangent(g6,g7) = 1.5708
    c: Coincident(g7,g8)
    c: Perpendicular(g8,g9) = 4.71239
    c: Coincident(g9,g0)
    c: Coincident(g7,g9)
    c: PointOnObject(g6,g0)
    c: Coincident(g10,g0)
    c: Coincident(g10,g6)
    c: Vertical(g11)
    c: Coincident(g11,g12)
    c: Coincident(g12,g13)
    c: Coincident(g13,g11)
    c: Coincident(g14,g15)
    c: Horizontal(g15)
    c: Coincident(g15,g16)
    c: Coincident(g14,g16)
    c: Horizontal(g12)
    c: Equal(g14,g11)
    c: Equal(g15,g12)
    c: Equal(g16,g13)
    c: Coincident(g17,g11)
    c: Coincident(g17,g0)
    c: Coincident(g18,g12)
    c: Coincident(g19,g14)
    c: PointOnObject(g20,g1)
    c: Vertical(g20)
    c: Coincident(g21,g14)
    c: PointOnObject(g21,g4)
    c: Coincident(g15,g18)
    c: Coincident(g11,g20)
    c: Vertical(g21)
    c: Horizontal(g19)
    c: Horizontal(g17)
    c: Angle(g7) = 0.698132
    c: Equal(g10,g17)
    c: Equal(g17,g19)
    c: Equal(g18,g19)
    c: Equal(g17,g20)
    c: Parallel(g16,g3)
    c: Coincident(g22,g14)
    c: Equal(g21,g22)
    c: Perpendicular(g3,g22)
    c: DistanceX(g19,g19) = 6
    c: Coincident(g23,g3)
    c: Coincident(g23,g1)
    c: Equal(g23,g22)
    c: Equal(g19,g14)
    c: Radius(g9) = 6
    c: Horizontal(g23)
    c: Equal(g4,g1)
    c: DistanceX(g1,g1) = 9.5
    c: DistanceY(g5,g5) = 18
    c: Symmetric(g3,g2,g22)
    c: Horizontal(g18)
    c: Coincident(g24,g7)
    c: PointOnObject(g24,g5)
    c: Horizontal(g24)
    c: Symmetric(g24,g7,g25)
    c: PointOnObject(g-1,g24)
    c: DistanceX(g25,g-1) = 3
FEATURE [PartDesign::Pocket] Pocket005  label="sigil_identation"
  BaseFeature = -> Pocket003
  Length = 0.75
  Length2 = 100
  Placement = pos=(-3e-15,-7.25,5e-15) rot=(0.57735,0.57735,-0.57735;2.0944rad)
  Profile = -> Sketch013
  Refine = true
  Type = 0
FEATURE [Sketcher::SketchObject] Sketch014
  ExternalGeometry = -> [Pocket005]
  MapMode = 5
  Placement = pos=(7.9e-15,-7.25,24.75) rot=(1,0,0;3.14159rad)
  Support = -> [Pocket005]
  sketch-geometry (5):
    g0: LineSegment StartX=5 StartY=-9 StartZ=0 EndX=-5 EndY=-9 EndZ=0
    g1: LineSegment StartX=-5 StartY=-9 StartZ=0 EndX=-5 EndY=-7 EndZ=0
    g2: LineSegment StartX=-5 StartY=-7 StartZ=0 EndX=5 EndY=-7 EndZ=0
    g3: LineSegment StartX=5 StartY=-7 StartZ=0 EndX=5 EndY=-9 EndZ=0
    g4: LineSegment [constr] StartX=5 StartY=-7 StartZ=0 EndX=5 EndY=-6.5 EndZ=0
  constraints (13):
    c: Coincident(g0,g1)
    c: Coincident(g1,g2)
    c: Coincident(g2,g3)
    c: Coincident(g3,g0)
    c: Vertical(g1)
    c: Vertical(g3)
    c: DistanceY(g3,g3) = 2
    c: Equal(g1,g3)
    c: Coincident(g4,g2)
    c: Vertical(g4)
    c: Coincident(g4,g-3)
    c: Symmetric(g1,g2,g-2)
    c: DistanceY(g4,g4) = 0.5
FEATURE [PartDesign::Pad] Pad009  label="board_tab"
  BaseFeature = -> Pocket005
  Length = 1
  Length2 = 100
  Placement = pos=(-3e-15,-7.25,5e-15) rot=(0.57735,0.57735,-0.57735;2.0944rad)
  Profile = -> Sketch014
  Refine = true
  Type = 0
FEATURE [PartDesign::AdditiveSphere] Sphere
  Angle1 = -90
  Angle2 = 90
  Angle3 = 360
  AttacherType = Attacher::AttachEngine3D
  BaseFeature = -> Pocket
  MapMode = 45
  Placement = pos=(7.4,-7.25,21.25) rot=(0.57735,0.57735,0.57735;4.18879rad)
  Radius = 1.25
  Refine = true
  Support = -> [Pocket]
FEATURE [PartDesign::AdditiveSphere] Sphere001
  Angle1 = -90
  Angle2 = 90
  Angle3 = 360
  AttacherType = Attacher::AttachEngine3D
  BaseFeature = -> Sphere
  MapMode = 45
  Placement = pos=(-7.4,-7.25,21.25) rot=(0.57735,0.57735,0.57735;4.18879rad)
  Radius = 1.25
  Refine = true
  Support = -> [Sphere]
FEATURE [PartDesign::Body] Body  label="buttons"
  Group = -> [Sketch,Pad,Sketch001,Pocket,Sphere,Sphere001]
  Origin = -> Origin002
  Tip = -> Sphere001
FEATURE [Sketcher::SketchObject] Sketch015
  ExternalGeometry = -> [Pad009]
  MapMode = 5
  Placement = pos=(-3e-15,-7.25,5e-15) rot=(-0.57735,-0.57735,0.57735;4.18879rad)
  Support = -> [Pad009]
  sketch-geometry (4):
    g0: LineSegment StartX=26.75 StartY=-15.25 StartZ=0 EndX=3.25 EndY=-15.25 EndZ=0
    g1: LineSegment StartX=3.25 StartY=-15.25 StartZ=0 EndX=7.75 EndY=-19.75 EndZ=0
    g2: LineSegment StartX=7.75 StartY=-19.75 StartZ=0 EndX=26.75 EndY=-19.75 EndZ=0
    g3: LineSegment StartX=26.75 StartY=-19.75 StartZ=0 EndX=26.75 EndY=-15.25 EndZ=0
  constraints (11):
    c: Horizontal(g0)
    c: Coincident(g1,g2)
    c: Horizontal(g2)
    c: Coincident(g2,g3)
    c: Vertical(g3)
    c: DistanceY(g3,g3) = 4.5
    c: Coincident(g0,g1)
    c: Angle(g-3,g1) = 2.35619
    c: Coincident(g3,g-3)
    c: Coincident(g0,g3)
    c: DistanceX(g2,g2) = 19
FEATURE [PartDesign::Pad] Pad010
  BaseFeature = -> Pad009
  Length = 42
  Length2 = 100
  Placement = pos=(-3e-15,-7.25,5e-15) rot=(0.57735,0.57735,-0.57735;2.0944rad)
  Profile = -> Sketch015
  Refine = true
  Reversed = true
  Type = 0
FEATURE [Sketcher::SketchObject] Sketch016
  ExternalGeometry = -> [Pad010]
  MapMode = 5
  Placement = pos=(1.625e-13,34.75,-4.17e-14) rot=(-0.57735,0.57735,0.57735;2.0944rad)
  Support = -> [Pad010]
  sketch-geometry (5):
    g0: LineSegment [constr] StartX=3.25 StartY=15.25 StartZ=0 EndX=26.75 EndY=15.25 EndZ=0
    g1: LineSegment StartX=26.75 StartY=15.25 StartZ=0 EndX=26.75 EndY=17.75 EndZ=0
    g2: LineSegment StartX=26.75 StartY=17.75 StartZ=0 EndX=8.57843 EndY=17.75 EndZ=0
    g3: LineSegment StartX=8.57843 StartY=17.75 StartZ=0 EndX=6.07843 EndY=15.25 EndZ=0
    g4: LineSegment StartX=6.07843 StartY=15.25 StartZ=0 EndX=26.75 EndY=15.25 EndZ=0
  constraints (14):
    c: Coincident(g0,g-5)
    c: Horizontal(g0)
    c: PointOnObject(g0,g-6)
    c: Coincident(g0,g1)
    c: PointOnObject(g1,g-6)
    c: Coincident(g1,g2)
    c: Horizontal(g2)
    c: Coincident(g2,g3)
    c: PointOnObject(g3,g0)
    c: Coincident(g3,g4)
    c: Coincident(g4,g1)
    c: Parallel(g3,g-3)
    c: DistanceY(g1,g-6) = 2
    c: Distance(g2,g-3) = 2
FEATURE [PartDesign::Pocket] Pocket006
  BaseFeature = -> Pad010
  Length = 40
  Length2 = 100
  Placement = pos=(-3e-15,-7.25,5e-15) rot=(0.57735,0.57735,-0.57735;2.0944rad)
  Profile = -> Sketch016
  Refine = true
  Type = 0
FEATURE [PartDesign::Body] Body001  label="case"
  Group = -> [Sketch002,Pad001,Sketch003,Pad002,Sketch004,Pad003,Sketch005,Pad004,Sketch006,Pocket001,Sketch008,Pocket002,Sketch010,Pocket003,Sketch013,Pocket005,Sketch014,Pad009,Sketch015,Pad010,Sketch016,Pocket006]
  Origin = -> Origin003
  Tip = -> Pocket006
FEATURE [Sketcher::SketchObject] Sketch017
  MapMode = 5
  Placement = pos=(0,0,0) rot=(0,0.707107,0.707107;3.14159rad)
  Support = -> [XZ_Plane005]
  sketch-geometry (10):
    g0: LineSegment StartX=15.4 StartY=-11.9 StartZ=0 EndX=15.4 EndY=-26.9 EndZ=0
    g1: LineSegment StartX=15.4 StartY=-26.9 StartZ=0 EndX=9 EndY=-26.9 EndZ=0
    g2: LineSegment StartX=9 StartY=-26.9 StartZ=0 EndX=9 EndY=-29.9 EndZ=0
    g3: LineSegment StartX=9 StartY=-29.9 StartZ=0 EndX=22.05 EndY=-29.9 EndZ=0
    g4: LineSegment StartX=22.05 StartY=-29.9 StartZ=0 EndX=22.05 EndY=-10.05 EndZ=0
    g5: LineSegment StartX=22.05 StartY=-10.05 StartZ=0 EndX=19.9 EndY=-7.9 EndZ=0
    g6: LineSegment StartX=19.9 StartY=-7.9 StartZ=0 EndX=19.9 EndY=-26.9 EndZ=0
    g7: LineSegment StartX=19.9 StartY=-26.9 StartZ=0 EndX=17.4 EndY=-26.9 EndZ=0
    g8: LineSegment StartX=17.4 StartY=-26.9 StartZ=0 EndX=17.4 EndY=-11.9 EndZ=0
    g9: LineSegment StartX=17.4 StartY=-11.9 StartZ=0 EndX=15.4 EndY=-11.9 EndZ=0
  constraints (30):
    c: Vertical(g0)
    c: Coincident(g0,g1)
    c: Horizontal(g1)
    c: Coincident(g1,g2)
    c: Coincident(g2,g3)
    c: Horizontal(g3)
    c: Coincident(g3,g4)
    c: Vertical(g4)
    c: Coincident(g4,g5)
    c: Coincident(g5,g6)
    c: Vertical(g6)
    c: Coincident(g6,g7)
    c: Horizontal(g7)
    c: Coincident(g7,g8)
    c: Vertical(g8)
    c: Coincident(g8,g9)
    c: Coincident(g9,g0)
    c: Vertical(g2)
    c: Horizontal(g9)
    c: DistanceX(g9,g9) = 2
    c: Equal(g8,g0)
    c: DistanceY(g2,g2) = 3
    c: DistanceY(g8,g8) = 15
    c: DistanceX(g1,g1) = 6.4
    c: DistanceY(g1,g-1) = 26.9
    c: Angle(g6,g5) = 0.785398
    c: DistanceY(g6,g6) = 19
    c: DistanceX(g7,g7) = 2.5
    c: Distance(g6,g4) = 2.15
    c: DistanceX(g-2,g1) = 9
FEATURE [Part::Feature] Shape001
  Placement = pos=(-26.9,52.9,58.3) rot=(1,0,0;3.14159rad)
  shape: bbox 22.5 x 8 x 5 mm, 19 faces (baked)
FEATURE [Part::MultiFuse] Fusion001  label="full_servo"
  Placement = pos=(3e-15,14.2,-11.2) rot=(0,0.707107,0.707107;3.14159rad)
  Refine = true
  Shapes = -> [Shape001,Shape]
FEATURE [PartDesign::Pad] Pad011
  Length = 34
  Length2 = 10
  Placement = pos=(0,0,0) rot=(1,0,0;1.5708rad)
  Profile = -> Sketch017
  Refine = true
  Type = 0
FEATURE [PartDesign::Body] Body003  label="mount"
  Group = -> [Sketch017,Pad011]
  Origin = -> Origin005
  Placement = pos=(0,-4.1,0) rot=(0,0,1;0rad)
  Tip = -> Pad011
FEATURE [Part::FeaturePython] Screw001  label="M3x8-Screw"  # Fasteners workbench fastener (typed FeaturePython)
  Placement = pos=(0,53.35,5.35) rot=(-1,0,0;1.5708rad)
  diameter = 1
  invert = false
  length = 3
  lengthCustom = 4
  matchOuter = true
  offset = 0
  thread = false
  type = 0
FEATURE [Sketcher::SketchObject] Sketch019  label="base"
  MapMode = 5
  Placement = pos=(0,49.85,5.35) rot=(0,0.707107,0.707107;3.14159rad)
  sketch-geometry (4):
    g0: ArcOfCircle CenterX=1.375e-13 CenterY=1.0001e-12 CenterZ=0 NormalX=0 NormalY=0 NormalZ=1 AngleXU=0 Radius=6 StartAngle=0.785398 EndAngle=5.49779
    g1: LineSegment StartX=4.24264 StartY=4.24264 StartZ=0 EndX=39.5741 EndY=4.24264 EndZ=0
    g2: LineSegment StartX=4.24264 StartY=-4.24264 StartZ=0 EndX=39.5741 EndY=-4.24264 EndZ=0
    g3: LineSegment StartX=39.5741 StartY=4.24264 StartZ=0 EndX=39.5741 EndY=-4.24264 EndZ=0
  constraints (11):
    c: Coincident(g0,g-1)
    c: Symmetric(g0,g0,g-1)
    c: Angle(g0) = 4.71239
    c: Radius(g0) = 6
    c: Coincident(g1,g0)
    c: Horizontal(g1)
    c: Coincident(g2,g0)
    c: Horizontal(g2)
    c: Coincident(g3,g1)
    c: Coincident(g3,g2)
    c: Vertical(g3)
FEATURE [Mesh::Feature] DiodoLaser
  Placement = pos=(-29.6,47.4,5.4) rot=(0.57735,-0.57735,-0.57735;2.0944rad)
FEATURE [PartDesign::Pad] Pad012  label="arm base"
  Length = 7
  Length2 = 100
  Placement = pos=(0,49.85,5.35) rot=(0,0.707107,0.707107;3.14159rad)
  Profile = -> Sketch019
  Refine = true
  Reversed = true
  Type = 0
FEATURE [Sketcher::SketchObject] Sketch020
  MapMode = 5
  Placement = pos=(-39.5741,49.85,5.35) rot=(0,-1,0;1.5708rad)
  Support = -> [Pad012]
  sketch-geometry (1):
    g0: Circle CenterX=0 CenterY=-2.5 CenterZ=0 NormalX=0 NormalY=0 NormalZ=1 AngleXU=0 Radius=3.25
  constraints (3):
    c: Radius(g0) = 3.25
    c: PointOnObject(g0,g-2)
    c: DistanceY(g-1,g0) = -2.5
FEATURE [PartDesign::Pocket] Pocket007  label="Laser Opening"
  BaseFeature = -> Pad012
  Length = 15
  Length2 = 100
  Placement = pos=(0,49.85,5.35) rot=(0,0.707107,0.707107;3.14159rad)
  Profile = -> Sketch020
  Refine = true
  Type = 0
FEATURE [Sketcher::SketchObject] Sketch021
  MapMode = 5
  Placement = pos=(-24.5741,49.85,5.35) rot=(0,-1,0;1.5708rad)
  Support = -> [Pocket007]
  sketch-geometry (4):
    g0: LineSegment StartX=-2.75 StartY=-0.75 StartZ=0 EndX=2.75 EndY=-0.75 EndZ=0
    g1: LineSegment StartX=2.75 StartY=-0.75 StartZ=0 EndX=2.75 EndY=-3.75 EndZ=0
    g2: LineSegment StartX=2.75 StartY=-3.75 StartZ=0 EndX=-2.75 EndY=-3.75 EndZ=0
    g3: LineSegment StartX=-2.75 StartY=-3.75 StartZ=0 EndX=-2.75 EndY=-0.75 EndZ=0
  constraints (11):
    c: Coincident(g0,g1)
    c: Coincident(g1,g2)
    c: Coincident(g2,g3)
    c: Coincident(g3,g0)
    c: Horizontal(g2)
    c: Vertical(g1)
    c: Vertical(g3)
    c: Symmetric(g0,g0,g-2)
    c: DistanceX(g0,g0) = 5.5
    c: Distance(g-1,g0) = 0.75
    c: DistanceY(g1,g1) = 3
FEATURE [Sketcher::SketchObject] Sketch022
  MapMode = 5
  Placement = pos=(-6e-16,42.85,5.35) rot=(0,-0.707107,0.707107;3.14159rad)
  Support = -> [Pad012]
  sketch-geometry (1):
    g0: Circle CenterX=0 CenterY=0 CenterZ=0 NormalX=0 NormalY=0 NormalZ=1 AngleXU=0 Radius=1.5
  constraints (2):
    c: Coincident(g0,g-1)
    c: Radius(g0) = 1.5
FEATURE [PartDesign::Pocket] Pocket009
  BaseFeature = -> Pocket007
  Length = 13
  Length2 = 100
  Placement = pos=(0,49.85,5.35) rot=(0,0.707107,0.707107;3.14159rad)
  Profile = -> Sketch022
  Refine = true
  Type = 0
FEATURE [Sketcher::SketchObject] Sketch023
  MapMode = 5
  Placement = pos=(-6e-16,42.85,5.35) rot=(0,-0.707107,0.707107;3.14159rad)
  Support = -> [Pocket009]
  sketch-geometry (6):
    g0: ArcOfCircle CenterX=16.9481 CenterY=-6.97357e-11 CenterZ=0 NormalX=0 NormalY=0 NormalZ=1 AngleXU=0 Radius=2 StartAngle=4.86353 EndAngle=7.70284
    g1: LineSegment StartX=17.2492 StartY=1.9772 StartZ=0 EndX=0.685384 EndY=4.5 EndZ=0
    g2: LineSegment StartX=17.2492 StartY=-1.9772 StartZ=0 EndX=0.685384 EndY=-4.5 EndZ=0
    g3: ArcOfCircle CenterX=-2.6097e-12 CenterY=-4.233e-13 CenterZ=0 NormalX=0 NormalY=0 NormalZ=1 AngleXU=0 Radius=4.5519 StartAngle=1.41965 EndAngle=4.86353
    g4: GeomPoint X=18.9481 Y=-5e-16 Z=0
    g5: GeomPoint X=-4.5519 Y=2e-15 Z=0
  constraints (13):
    c: Symmetric(g1,g2,g-1)
    c: PointOnObject(g4,g0)
    c: PointOnObject(g4,g-1)
    c: PointOnObject(g5,g3)
    c: PointOnObject(g5,g-1)
    c: DistanceY(g-1,g1) = 4.5
    c: Tangent(g1,g3) = -1.5708
    c: Tangent(g2,g3) = 1.5708
    c: Tangent(g0,g2) = 1.5708
    c: Tangent(g0,g1) = -1.5708
    c: DistanceX(g5,g4) = 23.5
    c: Radius(g0) = 2
    c: Coincident(g3,g-1)
FEATURE [PartDesign::Body] Body005
  Origin = -> Origin007
FEATURE [Sketcher::SketchObject] Sketch024
  AttachmentOffset = pos=(0,0,7.3) rot=(0,0,1;0rad)
  MapMode = 5
  Placement = pos=(0,-7.3,-1.6e-15) rot=(1,0,0;1.5708rad)
  Support = -> [XZ_Plane008]
  sketch-geometry (4):
    g0: LineSegment StartX=-21.75 StartY=-18.61 StartZ=0 EndX=15.25 EndY=-18.61 EndZ=0
    g1: LineSegment StartX=15.25 StartY=-18.61 StartZ=0 EndX=15.25 EndY=-40.61 EndZ=0
    g2: LineSegment StartX=15.25 StartY=-40.61 StartZ=0 EndX=-21.75 EndY=-40.61 EndZ=0
    g3: LineSegment StartX=-21.75 StartY=-40.61 StartZ=0 EndX=-21.75 EndY=-18.61 EndZ=0
  constraints (12):
    c: Coincident(g0,g1)
    c: Coincident(g1,g2)
    c: Coincident(g2,g3)
    c: Coincident(g3,g0)
    c: Horizontal(g0)
    c: Horizontal(g2)
    c: Vertical(g1)
    c: Vertical(g3)
    c: DistanceY(g3,g3) = 22
    c: DistanceX(g2,g2) = 37
    c: DistanceX(g0) = 15.25
    c: DistanceY(g0) = -18.61
FEATURE [PartDesign::Pad] Pad013
  Length = 2
  Length2 = 100
  Placement = pos=(0,0,0) rot=(1,0,0;1.5708rad)
  Profile = -> Sketch024
  Refine = true
  Type = 0
FEATURE [Sketcher::SketchObject] Sketch025
  ExternalGeometry = -> [Sketch024]
  MapMode = 5
  Placement = pos=(0,-7.3,3.1e-15) rot=(-1,0,0;1.5708rad)
  Support = -> [Pad013]
  sketch-geometry (4):
    g0: LineSegment StartX=-21.75 StartY=27.11 StartZ=0 EndX=15.25 EndY=27.11 EndZ=0
    g1: LineSegment StartX=15.25 StartY=27.11 StartZ=0 EndX=15.25 EndY=29.11 EndZ=0
    g2: LineSegment StartX=15.25 StartY=29.11 StartZ=0 EndX=-21.75 EndY=29.11 EndZ=0
    g3: LineSegment StartX=-21.75 StartY=29.11 StartZ=0 EndX=-21.75 EndY=27.11 EndZ=0
  constraints (12):
    c: Coincident(g0,g1)
    c: Coincident(g1,g2)
    c: Coincident(g2,g3)
    c: Coincident(g3,g0)
    c: Horizontal(g0)
    c: Horizontal(g2)
    c: Vertical(g1)
    c: Vertical(g3)
    c: DistanceY(g3,g3) = 2
    c: DistanceX(g2,g2) = 37
    c: PointOnObject(g2,g-3)
    c: DistanceY(g-3,g0) = 8.5
FEATURE [PartDesign::Pad] Pad014
  BaseFeature = -> Pad013
  Length = 38
  Length2 = 103
  Placement = pos=(0,0,0) rot=(1,0,0;1.5708rad)
  Profile = -> Sketch025
  Refine = true
  Type = 0
FEATURE [Sketcher::SketchObject] Sketch027
  ExternalGeometry = -> [Sketch024,Pad014]
  MapMode = 5
  Placement = pos=(0,-3.15e-14,-27.11) rot=(0,0,1;3.14159rad)
  Support = -> [Pad014]
  sketch-geometry (4):
    g0: LineSegment StartX=15.6 StartY=4.5 StartZ=0 EndX=17.35 EndY=4.5 EndZ=0
    g1: LineSegment StartX=17.35 StartY=4.5 StartZ=0 EndX=17.35 EndY=-7.5 EndZ=0
    g2: LineSegment StartX=17.35 StartY=-7.5 StartZ=0 EndX=15.6 EndY=-7.5 EndZ=0
    g3: LineSegment StartX=15.6 StartY=-7.5 StartZ=0 EndX=15.6 EndY=4.5 EndZ=0
  constraints (12):
    c: Coincident(g0,g1)
    c: Coincident(g1,g2)
    c: Coincident(g2,g3)
    c: Coincident(g3,g0)
    c: Horizontal(g0)
    c: Horizontal(g2)
    c: Vertical(g1)
    c: Vertical(g3)
    c: DistanceX(g0,g0) = 1.75
    c: DistanceX(g0) = 17.35
    c: DistanceY(g-1,g0) = 4.5
    c: DistanceY(g3,g3) = 12
FEATURE [PartDesign::Pad] Pad015
  BaseFeature = -> Pad014
  Length = 5
  Length2 = 100
  Placement = pos=(0,0,0) rot=(1,0,0;1.5708rad)
  Profile = -> Sketch027
  Refine = true
  Type = 0
FEATURE [PartDesign::Body] Body006  label="v2_mount"
  Group = -> [Sketch024,Pad013,Sketch025,Pad014,Sketch027,Pad015]
  Origin = -> Origin008
  Tip = -> Pad015
FEATURE [PartDesign::Pocket] Pocket010  label="horn hole"
  BaseFeature = -> Pocket009
  Length = 4.1
  Length2 = 100
  Placement = pos=(0,49.85,5.35) rot=(0,0.707107,0.707107;3.14159rad)
  Profile = -> Sketch023
  Refine = true
  Type = 0
FEATURE [Sketcher::SketchObject] Sketch029  label="hollow path"
  MapMode = 5
  Support = -> [XY_Plane006]
  sketch-geometry (3):
    g0: ArcOfCircle CenterX=-8.95173 CenterY=55.714 CenterZ=0 NormalX=0 NormalY=0 NormalZ=1 AngleXU=0 Radius=6.02687 StartAngle=4.72064 EndAngle=5.5654
    g1: LineSegment StartX=-8.90199 StartY=49.6873 StartZ=0 EndX=-24.5815 EndY=48.3511 EndZ=0
    g2: GeomPoint X=-11 Y=51.75 Z=0
  constraints (5):
    c: Coincident(g0,g1)
    c: DistanceY(g0) = 51.75
    c: DistanceX(g2) = -11
    c: DistanceY(g2) = 51.75
    c: DistanceX(g0) = -4.41191
FEATURE [PartDesign::SubtractivePipe] SubtractivePipe
  AuxilleryCurvelinear = true
  AuxillerySpineTangent = false
  BaseFeature = -> Pocket010
  Binormal = (0,0,0)
  Mode = 0
  Placement = pos=(0,49.85,5.35) rot=(0,0.707107,0.707107;3.14159rad)
  Profile = -> Sketch021
  Refine = true
  Spine = -> Sketch029
  SpineTangent = false
  Transformation = 0
  Transition = 0
FEATURE [Sketcher::SketchObject] Sketch030
  MapMode = 5
  Placement = pos=(-39.5741,49.85,5.35) rot=(0,-1,0;1.5708rad)
  Support = -> [SubtractivePipe]
  sketch-geometry (4):
    g0: LineSegment StartX=-3.25 StartY=-0.9 StartZ=0 EndX=3.25 EndY=-0.9 EndZ=0
    g1: LineSegment StartX=3.25 StartY=-0.9 StartZ=0 EndX=3.25 EndY=-4.15 EndZ=0
    g2: LineSegment StartX=3.25 StartY=-4.15 StartZ=0 EndX=-3.25 EndY=-4.15 EndZ=0
    g3: LineSegment StartX=-3.25 StartY=-4.15 StartZ=0 EndX=-3.25 EndY=-0.9 EndZ=0
  constraints (11):
    c: Coincident(g0,g1)
    c: Coincident(g1,g2)
    c: Coincident(g2,g3)
    c: Coincident(g3,g0)
    c: Horizontal(g2)
    c: Vertical(g1)
    c: Vertical(g3)
    c: Symmetric(g0,g0,g-2)
    c: DistanceX(g0,g0) = 6.5
    c: DistanceY(g-1,g0) = -0.9
    c: DistanceY(g1,g1) = 3.25
FEATURE [PartDesign::Pocket] Pocket011
  BaseFeature = -> SubtractivePipe
  Length = 15
  Length2 = 100
  Placement = pos=(0,49.85,5.35) rot=(0,0.707107,0.707107;3.14159rad)
  Profile = -> Sketch030
  Refine = true
  Type = 0
FEATURE [PartDesign::Body] Body004  label="Arm"
  Group = -> [Screw001,Sketch019,Pad012,Sketch020,Pocket007,Sketch022,Pocket009,Sketch023,Pocket010,Sketch021,Sketch029,SubtractivePipe,Sketch030,Pocket011]
  Origin = -> Origin006
  Tip = -> Pocket011
FEATURE [App::Part] Part  label="Parts"
  Group = -> [Body,Body002,Body001,Body003,Body004,Body005,Body006]
  Origin = -> Origin001
